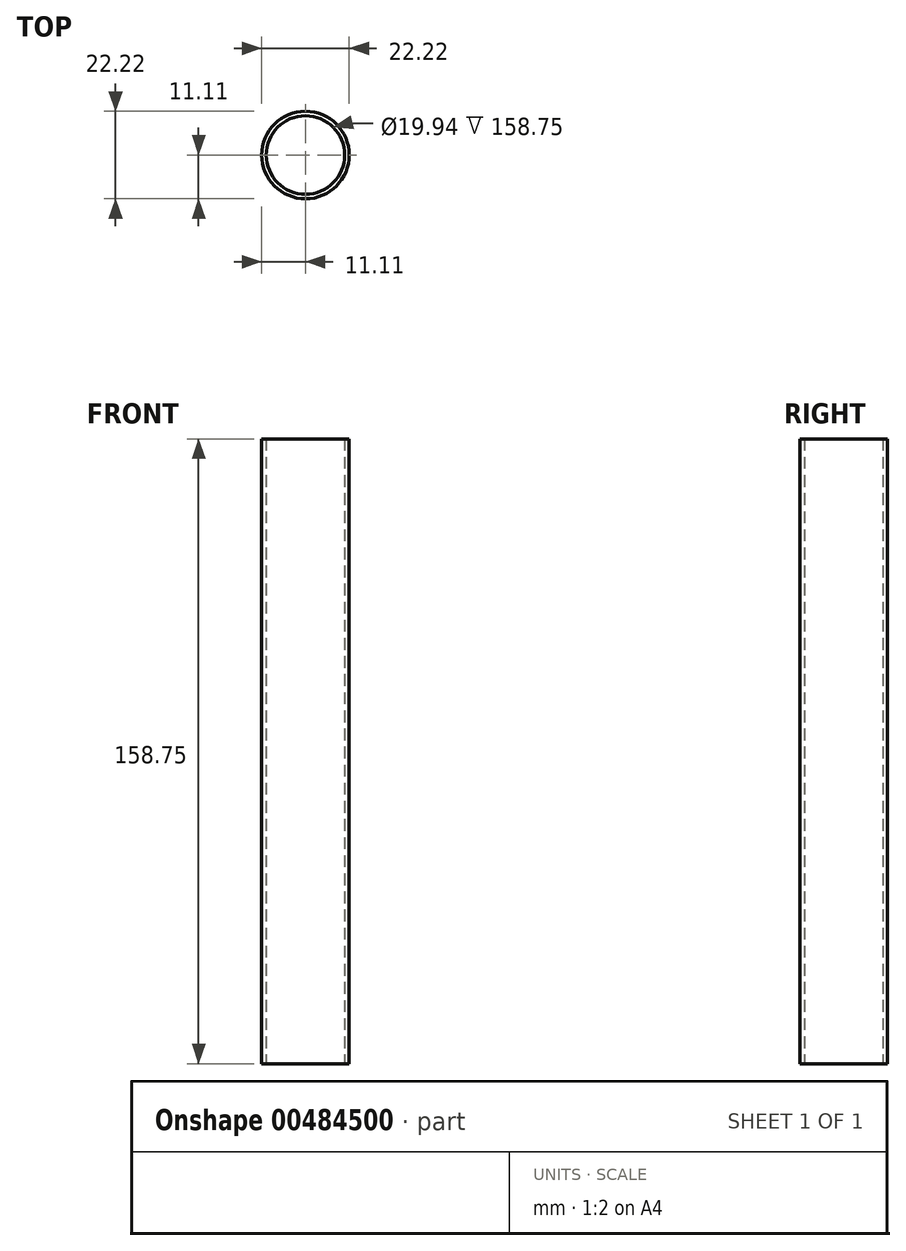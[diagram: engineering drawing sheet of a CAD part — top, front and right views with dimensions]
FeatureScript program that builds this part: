
annotation { "Feature Type Name" : "Feature", "Feature Type Description" : "" }
export const myFeature = defineFeature(function(context is Context, id is Id, definition is map)
    precondition{}
    {
        {
            var Q0;
            Q0=qCreatedBy(makeId("Top.planeOp"),FACE);
            var sketch = newSketch(context, id + "F0", { "sketchPlane" : qUnion([Q0])});
            skCircle(sketch, "E0", {"center": v(0, 0) * mm, "radius": 11.11 * mm});
            skCircle(sketch, "E1", {"center": v(0, 0) * mm, "radius": 9.97 * mm});
            skSolve(sketch);
        }
        {
            var Q0;
            Q0 = qSketchRegion(id + "F0", true);
            extrude(context, id + "F1", {"entities" : qUnion([Q0]), "depth" : 158.75 * mm});
        }
    });
